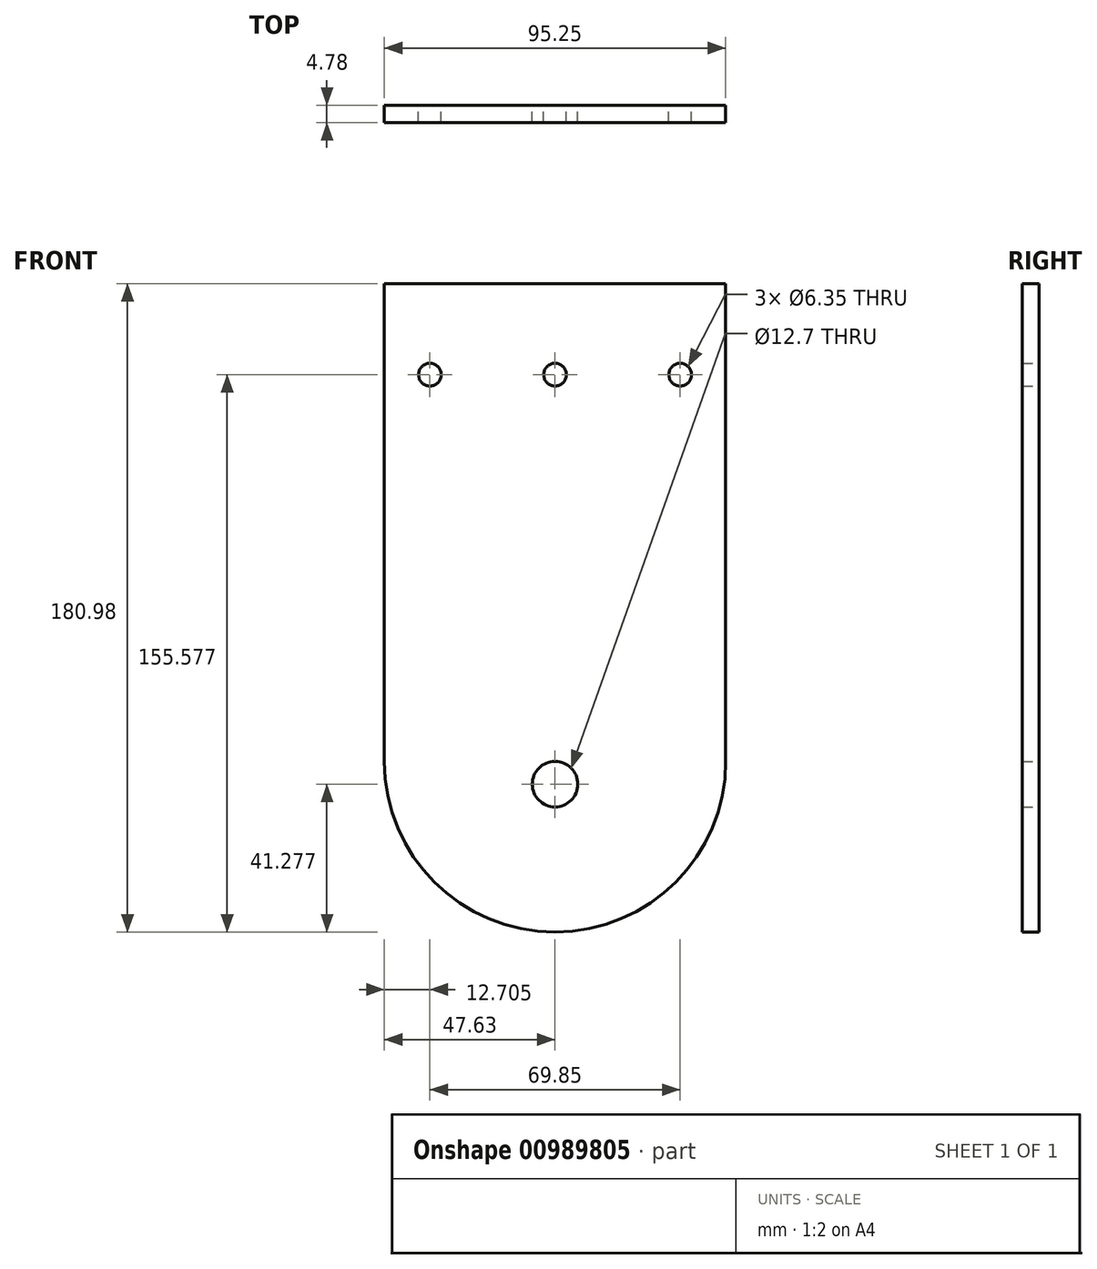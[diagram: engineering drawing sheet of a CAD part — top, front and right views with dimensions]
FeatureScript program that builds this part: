
annotation { "Feature Type Name" : "Feature", "Feature Type Description" : "" }
export const myFeature = defineFeature(function(context is Context, id is Id, definition is map)
    precondition{}
    {
        {
            var Q0;
            Q0=qCreatedBy(makeId("Front.planeOp"),FACE);
            var sketch = newSketch(context, id + "F0", { "sketchPlane" : qUnion([Q0])});
            skLineSegment(sketch, "E0.bottom", {"start": v(-47.63, 90.49) * mm, "end": v(47.63, 90.49) * mm});
            skLineSegment(sketch, "E0.top", {"start": v(0, -90.49) * mm, "end": v(0, -90.49) * mm});
            skLineSegment(sketch, "E0.left", {"start": v(-47.63, 90.49) * mm, "end": v(-47.63, -42.86) * mm});
            skLineSegment(sketch, "E0.right", {"start": v(47.63, 90.49) * mm, "end": v(47.63, -42.86) * mm});
            skPoint(sketch, "E1.visualSharp", {"position": v(47.63, -90.49) * mm});
            skArc(sketch, "E1.filletArc", {"start": v(0, -90.49) * mm, "mid": v(33.68, -76.54) * mm, "end": v(47.63, -42.86) * mm});
            skPoint(sketch, "E2.visualSharp", {"position": v(-47.63, -90.49) * mm});
            skArc(sketch, "E2.filletArc", {"start": v(-47.63, -42.86) * mm, "mid": v(-33.68, -76.54) * mm, "end": v(0, -90.49) * mm});
            skCircle(sketch, "E3", {"center": v(0, -49.21) * mm, "radius": 6.35 * mm});
            skCircle(sketch, "E4", {"center": v(-34.93, 65.09) * mm, "radius": 3.18 * mm});
            skCircle(sketch, "E5.1.0.0", {"center": v(0, 65.09) * mm, "radius": 3.18 * mm});
            skCircle(sketch, "E5.2.0.0", {"center": v(34.93, 65.09) * mm, "radius": 3.18 * mm});
            skLineSegment(sketch, "E5.direction1", {"start": v(-34.93, 65.09) * mm, "end": v(0, 65.09) * mm, "construction": true});
            skSolve(sketch);
        }
        {
            var Q0;
            Q0=makeQuery(id+"F0.imprint","IMPRINT",FACE,{"disambiguationData":[TD([[makeQuery(id+"F0.imprint","IMPRINT",EDGE,{"derivedFrom":sQuery(id+"F0.wireOp",EDGE,"E0.bottom")}),-1.0]])]});
            extrude(context, id + "F1", {"entities" : qUnion([Q0]), "depth" : 4.78 * mm, "offsetDistance" : 25.4 * mm});
        }
    });
